# Revit family: Building-SurfaceMountingEnclosures-GEWISS-44CE-JUNCTION-BOXES-WALL-MOUNTING_HIGH_LID
name_source: partatom
category: Apparecchi elettrici
revit_build: Autodesk Revit 2016 (Build: 20161004_0715(x64)
units: mm (PartAtom-declared; Revit-internal decimal feet)

## family parameters
Condiviso = No
Host = Superficie
Mantenere orientamento annotazione = Sì
Numero OmniClass = 23.80.30.14.24
Punto di calcolo locali = Sì
Quota connettore circolare = Usa diametro
Taglio con vuoti quando caricato = No
Tipo di parte = Normale
Titolo OmniClass = Junction Boxes

## types (1)
- Building-SurfaceMountingEnclosures-GEWISS-44CE-JUNCTION-BOXES-WALL-MOUNTING_HIGH_LID
    Accessories for insulation restoring = GW44621
    Application = Industrial uses
    Carico apparente = 0 VA
    Catalogue = BUILDING
    Catalogue Range = 44 CE
    Classificazione = Other
    Colour = Grey RAL 7035
    Coperchio = GEWISS COPERCHIO TRASPARENTE
    Descrizione = ENCLOSURE.W.TRASP.LID 460X380X180 IP56
    Dettaglio = Eemento di dettaglio - 44CE : 460x380x120
    EAN code = 8011564014206
    Electrocod = 0231
    GEWISS SCHEDA TECNICA = http://pro.gewiss.com
    Glow Wire Test = 650°C
    IDF = 68665031-5035-41bd-8052-329dc6ddcf46
    IDT = 238c3f26-d7fd-486c-9f58-b8ff1378d212
    IP degree = IP56
    Immagine tipo = GW44441.jpg
    Insulation class = II (according to IEC 61140 standards)
    Internal dim. LxHxD (mm) = 460x380x180
    Larghezza_interna = 460 mm  [stored 1.50919 ft]
    Lid = Deep screwed
    Lid colour = Transparent
    Lid screws (no. and type) = 6 insul. sealable hinged
    Lunghezza_interna = 380 mm
    Material = Technopolymer GWPLAST 120
    Max Ã˜ holes possible = 48MM
    Modello = GW44441
    Operating temperature = -25 +60 °C
    Produttore = GEWISS S.p.A.
    Prospetto di default = 1219 mm
    SEO = Box
    Scatola = GEWISS - Grigio RAL 7035
    Shock resistance = IK08
    Spessore = 180 mm  [stored 0.590551 ft]
    Technical sheet = https://www.gewiss.com
    Thermo-pressure with ball = 110
    Torque screws tightening = 1,8NM
    Type of material = Halogen-free in compliance with EN 60754-2
    URL = https://www.gewiss.com
    Version file RFA = 18.0
    Voltaggio_x = 0 V
    Walls = Smooth

note: source unit labels omitted for Thermo-pressure with ball — the stored unit's dimension contradicts the parameter name (converter mislabeling)

note: [stored X ft] marks values corroborated as IEEE doubles in the binary element streams (Revit-internal decimal feet)

## geometry (parser evidence)
native form markers: Blend x2, Sweep x2
no freeform markers — native parametric forms only
